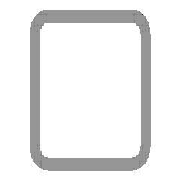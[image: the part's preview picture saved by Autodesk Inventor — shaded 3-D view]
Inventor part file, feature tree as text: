
AUTODESK INVENTOR PART (.ipt)
format: ipt  version: 2022 (Build 260153000, 153)  size: 133,120 bytes
history: native  units: mm (DEFAULTED — no unit token found)
features: other x4, sketch x3, plane x1
ambient origin geometry x8: Origin, YZ Plane, XZ Plane, XY Plane, X Axis, Y Axis, Z Axis, Center Point
bodies: Solid1 (feature_tree), Body (feature_tree)
feature tree (8):
  parser-record x1  (decoder bookkeeping rows leaked as tree rows — omitted from the tree; the rows remain in map.json)
  other  "Driven Length"
  other  "Start Plane"
  other  "End Plane"
  sketch  "Sketch"  dims[d7=8.0mm d9=40.0mm d11=40.0mm d12=4.0mm d13=-0.0mm d14=180.0mm d15=20.0mm d16=20.0mm d17=90.0deg d18=180.0mm]
  sketch  "Sketch3"  dims[d3=180.0mm]
  plane  "Work Plane3"
  sketch  "Sketch4"  dims[d4=0.0mm]
